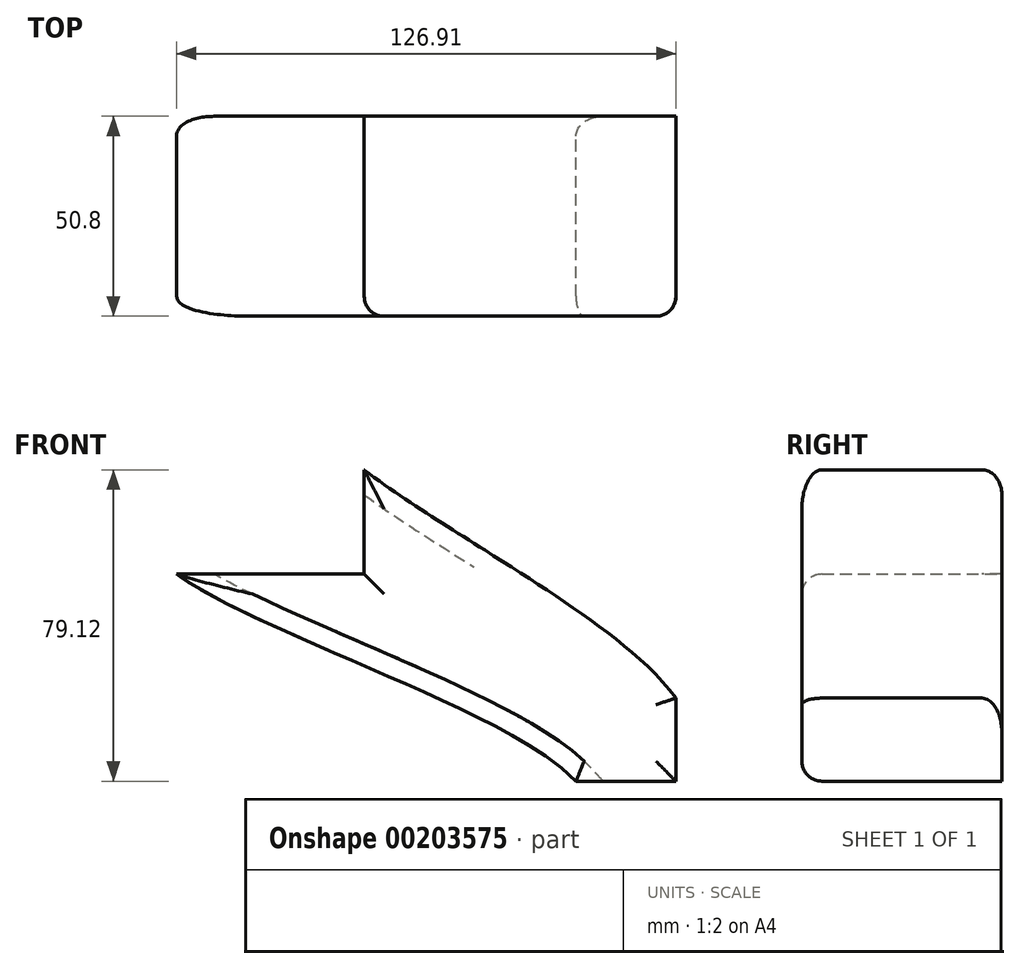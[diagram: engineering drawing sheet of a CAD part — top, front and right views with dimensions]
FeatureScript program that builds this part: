
annotation { "Feature Type Name" : "Feature", "Feature Type Description" : "" }
export const myFeature = defineFeature(function(context is Context, id is Id, definition is map)
    precondition{}
    {
        {
            var Q0;
            Q0=qCreatedBy(makeId("Front.planeOp"),FACE);
            var sketch = newSketch(context, id + "F0", { "sketchPlane" : qUnion([Q0])});
            skLineSegment(sketch, "E0.bottom", {"start": v(-56.56, 35.13) * mm, "end": v(-8.84, 35.13) * mm});
            skLineSegment(sketch, "E0.top", {"start": v(-56.56, 8.62) * mm, "end": v(-8.84, 8.62) * mm});
            skLineSegment(sketch, "E0.left", {"start": v(-56.56, 35.13) * mm, "end": v(-56.56, 8.62) * mm});
            skLineSegment(sketch, "E0.right", {"start": v(-8.84, 35.13) * mm, "end": v(-8.84, 8.62) * mm});
            skPoint(sketch, "E0.middle", {"position": v(-32.7, 21.87) * mm});
            skLineSegment(sketch, "E1.bottom", {"start": v(70.35, -43.99) * mm, "end": v(44.95, -43.99) * mm});
            skLineSegment(sketch, "E1.top", {"start": v(70.35, -22.89) * mm, "end": v(44.95, -22.89) * mm});
            skLineSegment(sketch, "E1.left", {"start": v(70.35, -43.99) * mm, "end": v(70.35, -22.89) * mm});
            skLineSegment(sketch, "E1.right", {"start": v(44.95, -43.99) * mm, "end": v(44.95, -22.89) * mm});
            skPoint(sketch, "E1.middle", {"position": v(57.65, -33.44) * mm});
            skFitSpline(sketch, "E2", {"points": [v(-8.84, 35.13) * mm, v(70.35, -22.89) * mm], "startDerivative": vector(62.3, -48.6) * mm, "endDerivative": vector(41.41, -58.28) * mm});
            skFitSpline(sketch, "E3", {"points": [v(21.79, 14.72) * mm, v(43.3, 26.29) * mm], "startDerivative": vector(21.4, 15.14) * mm, "endDerivative": vector(21.4, 15.14) * mm});
            skFitSpline(sketch, "E4", {"points": [v(-56.56, 8.62) * mm, v(44.95, -43.99) * mm], "startDerivative": vector(65.84, -46.84) * mm, "endDerivative": vector(49.58, -53.41) * mm});
            skSolve(sketch);
        }
        {
            var Q0;
            Q0=makeQuery(id+"F0.imprint","IMPRINT",FACE,{"disambiguationData":[TD([[makeQuery(id+"F0.imprint","IMPRINT",EDGE,{"derivedFrom":sQuery(id+"F0.wireOp",EDGE,"E1.bottom")}),-1.0]])]});
            var Q1;
            Q1=makeQuery(id+"F0.imprint","IMPRINT",FACE,{"disambiguationData":[TD([[makeQuery(id+"F0.imprint","IMPRINT",EDGE,{"derivedFrom":sQuery(id+"F0.wireOp",EDGE,"E0.top")}),-1.0]])]});
            extrude(context, id + "F1", {"entities" : qUnion([Q0, Q1]), "depth" : 50.8 * mm});
        }
        {
            var Q0;
            Q0=makeQuery(id+"F1.opExtrude","CAP_EDGE",EDGE,{"disambiguationData":[OSD([sQuery(id+"F0.wireOp",EDGE,"E4")])],"isStart":false});
            var Q1;
            Q1=makeQuery(id+"F1.opExtrude","CAP_EDGE",EDGE,{"disambiguationData":[OSD([sQuery(id+"F0.wireOp",EDGE,"E2")])],"isStart":false});
            var Q2;
            Q2=makeQuery(id+"F1.opExtrude","CAP_FACE",FACE,{"disambiguationData":[OSD([sQuery(id+"F0.wireOp",EDGE,"E0.top"),sQuery(id+"F0.wireOp",EDGE,"E0.right"),sQuery(id+"F0.wireOp",EDGE,"E1.bottom"),sQuery(id+"F0.wireOp",EDGE,"E1.left"),sQuery(id+"F0.wireOp",EDGE,"E2"),sQuery(id+"F0.wireOp",EDGE,"E4")])],"isStart":false});
            var Q3;
            Q3=makeQuery(id+"F1.opExtrude","CAP_EDGE",EDGE,{"disambiguationData":[OSD([sQuery(id+"F0.wireOp",EDGE,"E4")])],"isStart":true});
            var Q4;
            Q4=makeQuery(id+"F1.opExtrude","CAP_EDGE",EDGE,{"disambiguationData":[OSD([sQuery(id+"F0.wireOp",EDGE,"E2")])],"isStart":true});
            fillet(context, id + "F2", {"entities" : qUnion([Q0, Q1, Q2, Q3, Q4]), "radius" : 5.08 * mm, "tangentPropagation" : true, "allowEdgeOverflow" : false});
        }
    });
